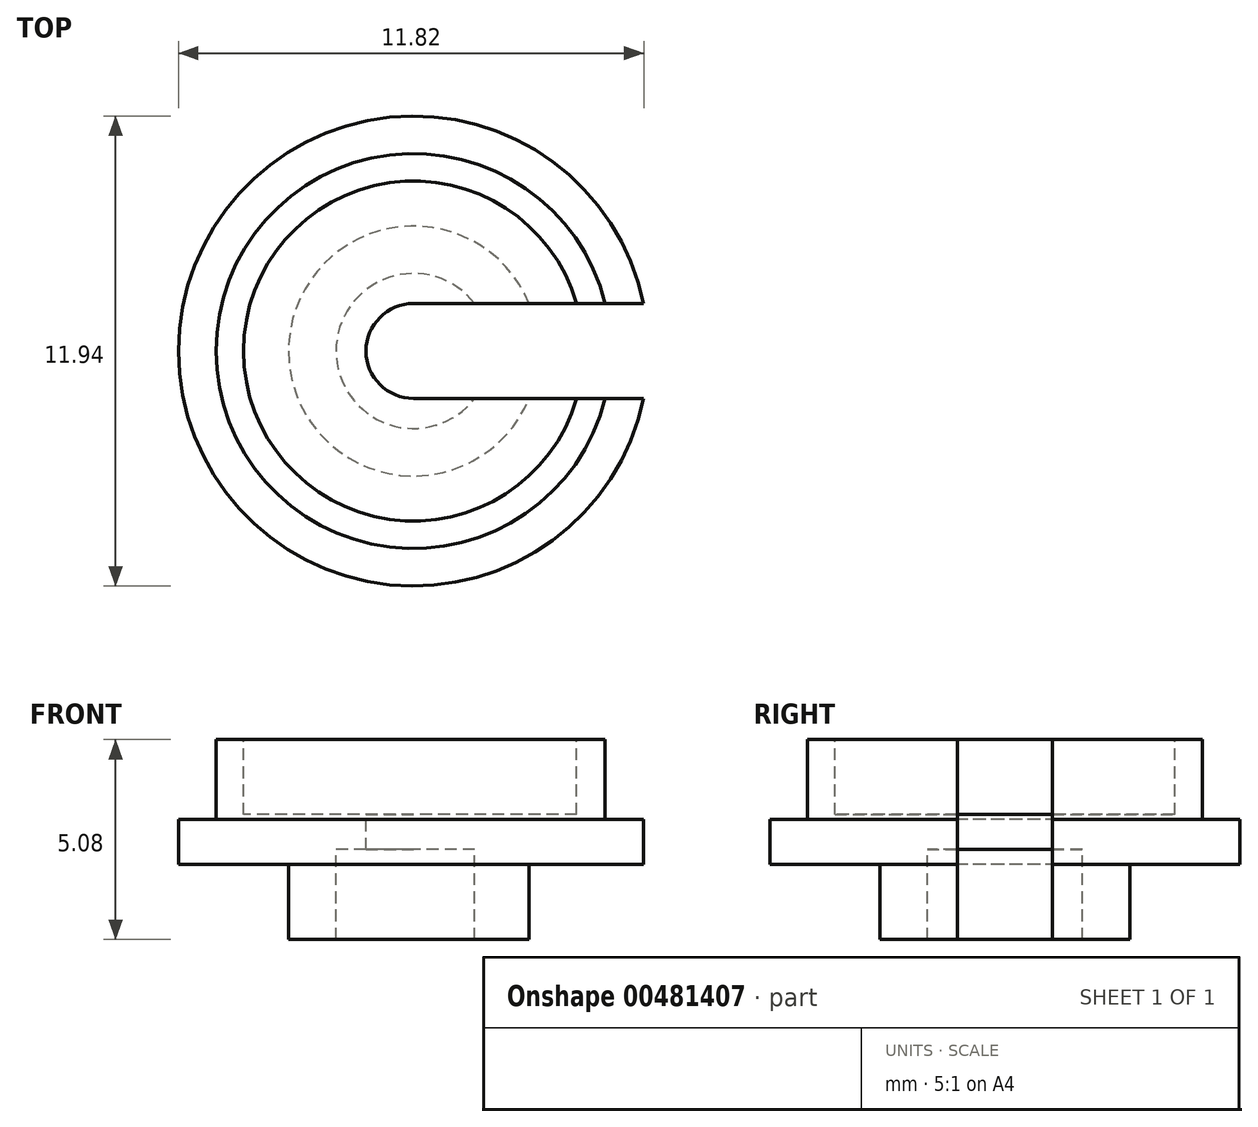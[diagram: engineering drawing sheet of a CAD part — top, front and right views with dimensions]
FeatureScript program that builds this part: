
annotation { "Feature Type Name" : "Feature", "Feature Type Description" : "" }
export const myFeature = defineFeature(function(context is Context, id is Id, definition is map)
    precondition{}
    {
        {
            var Q0;
            Q0=qCreatedBy(makeId("Front.planeOp"),FACE);
            var sketch = newSketch(context, id + "F0", { "sketchPlane" : qUnion([Q0])});
            skLineSegment(sketch, "E0", {"start": v(0, 3.2) * mm, "end": v(0, 0) * mm, "construction": true});
            skLineSegment(sketch, "E1", {"start": v(1.97, 0) * mm, "end": v(1.97, 2.29) * mm});
            skLineSegment(sketch, "E2", {"start": v(1.97, 2.29) * mm, "end": v(1.2, 2.29) * mm});
            skLineSegment(sketch, "E3", {"start": v(1.2, 2.29) * mm, "end": v(1.2, 3.17) * mm});
            skLineSegment(sketch, "E4", {"start": v(3.18, 0) * mm, "end": v(3.18, 1.9) * mm});
            skLineSegment(sketch, "E5", {"start": v(3.18, 0) * mm, "end": v(1.97, 0) * mm});
            skLineSegment(sketch, "E6", {"start": v(3.18, 1.9) * mm, "end": v(5.97, 1.9) * mm});
            skLineSegment(sketch, "E7", {"start": v(5.97, 1.9) * mm, "end": v(5.97, 3.05) * mm});
            skLineSegment(sketch, "E8", {"start": v(5.97, 3.05) * mm, "end": v(5.02, 3.05) * mm});
            skLineSegment(sketch, "E9", {"start": v(5.02, 3.05) * mm, "end": v(5.02, 5.08) * mm});
            skLineSegment(sketch, "E10", {"start": v(5.02, 5.08) * mm, "end": v(4.32, 5.08) * mm});
            skLineSegment(sketch, "E11", {"start": v(4.32, 5.08) * mm, "end": v(4.32, 3.18) * mm});
            skLineSegment(sketch, "E12", {"start": v(4.32, 3.18) * mm, "end": v(1.2, 3.18) * mm});
            skSolve(sketch);
        }
        {
            var Q0;
            Q0 = qSketchRegion(id + "F0", true);
            var Q1;
            Q1=sQuery(id+"F0.wireOp",EDGE,"E0");
            revolve(context, id + "F1", {"entities" : qUnion([Q0]), "axis" : qUnion([Q1]), "revolveType" : RevolveType.FULL});
        }
        {
            var Q0;
            Q0=qCreatedBy(makeId("Top.planeOp"),FACE);
            var sketch = newSketch(context, id + "F2", { "sketchPlane" : qUnion([Q0])});
            skArc(sketch, "E13.0", {"start": v(0, 1.2) * mm, "mid": v(-1.2, 0) * mm, "end": v(0, -1.2) * mm});
            skLineSegment(sketch, "E14", {"start": v(0, 1.2) * mm, "end": v(5.85, 1.2) * mm});
            skLineSegment(sketch, "E15", {"start": v(0, -1.2) * mm, "end": v(5.85, -1.2) * mm});
            skArc(sketch, "E16.0", {"start": v(5.85, -1.2) * mm, "mid": v(5.97, 0) * mm, "end": v(5.85, 1.2) * mm});
            skSolve(sketch);
        }
        {
            var Q0;
            Q0 = qSketchRegion(id + "F2", true);
            extrude(context, id + "F3", {"entities" : qUnion([Q0]), "operationType" : NewBodyOperationType.REMOVE, "endBound" : BoundingType.THROUGH_ALL, "oppositeDirection" : true, "depth" : 25.4 * mm, "hasSecondDirection" : true, "secondDirectionBound" : SecondDirectionBoundingType.THROUGH_ALL, "secondDirectionOppositeDirection" : false, "secondDirectionDepth" : 25.4 * mm});
        }
    });
